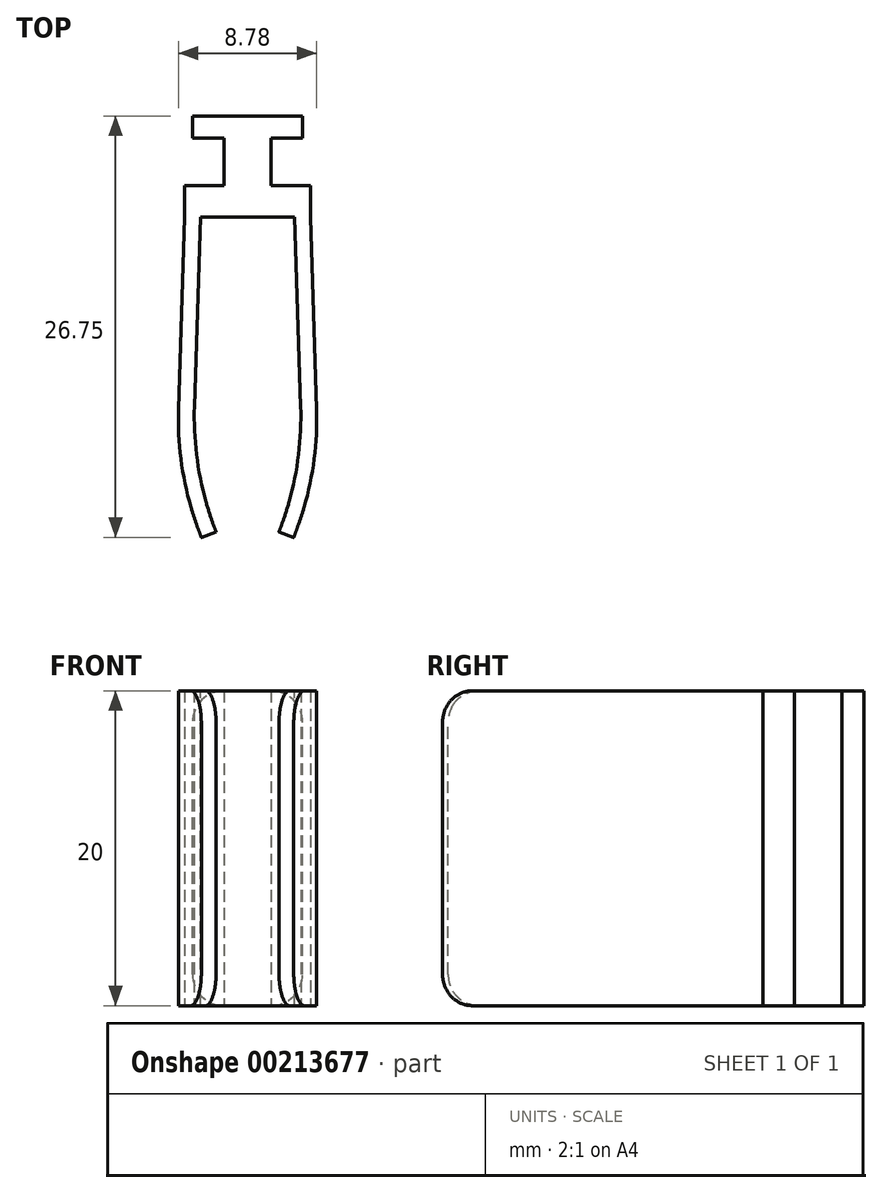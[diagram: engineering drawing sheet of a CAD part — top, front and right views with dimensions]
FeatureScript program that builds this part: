
annotation { "Feature Type Name" : "Feature", "Feature Type Description" : "" }
export const myFeature = defineFeature(function(context is Context, id is Id, definition is map)
    precondition{}
    {
        {
            var Q0;
            Q0=qCreatedBy(makeId("Front.planeOp"),FACE);
            var sketch = newSketch(context, id + "F0", { "sketchPlane" : qUnion([Q0])});
            skLineSegment(sketch, "E0.bottom", {"start": v(3.5, -10) * mm, "end": v(-3.5, -10) * mm});
            skLineSegment(sketch, "E0.top", {"start": v(3.5, 10) * mm, "end": v(-3.5, 10) * mm});
            skLineSegment(sketch, "E0.left", {"start": v(3.5, -10) * mm, "end": v(3.5, 10) * mm});
            skLineSegment(sketch, "E0.right", {"start": v(-3.5, -10) * mm, "end": v(-3.5, 10) * mm});
            skPoint(sketch, "E0.middle", {"position": v(0, 0) * mm});
            skSolve(sketch);
        }
        {
            var Q0;
            Q0=makeQuery(id+"F0.imprint","IMPRINT",FACE,{"disambiguationData":[TD([[makeQuery(id+"F0.imprint","IMPRINT",EDGE,{"derivedFrom":sQuery(id+"F0.wireOp",EDGE,"E0.bottom")}),-1.0]])]});
            extrude(context, id + "F1", {"entities" : qUnion([Q0]), "depth" : 1.4 * mm});
        }
        {
            var Q0;
            Q0=makeQuery(id+"F1.opExtrude","CAP_FACE",FACE,{"disambiguationData":[OSD([sQuery(id+"F0.wireOp",EDGE,"E0.bottom"),sQuery(id+"F0.wireOp",EDGE,"E0.top"),sQuery(id+"F0.wireOp",EDGE,"E0.left"),sQuery(id+"F0.wireOp",EDGE,"E0.right")])],"isStart":false});
            var sketch = newSketch(context, id + "F2", { "sketchPlane" : qUnion([Q0])});
            skLineSegment(sketch, "E1.bottom", {"start": v(1.5, 10) * mm, "end": v(-1.5, 10) * mm});
            skLineSegment(sketch, "E1.top", {"start": v(1.5, -10) * mm, "end": v(-1.5, -10) * mm});
            skLineSegment(sketch, "E1.left", {"start": v(1.5, 10) * mm, "end": v(1.5, -10) * mm});
            skLineSegment(sketch, "E1.right", {"start": v(-1.5, 10) * mm, "end": v(-1.5, -10) * mm});
            skPoint(sketch, "E1.middle", {"position": v(0, 0) * mm});
            skSolve(sketch);
        }
        {
            var Q0;
            Q0=makeQuery(id+"F2.imprint","IMPRINT",FACE,{"disambiguationData":[TD([[makeQuery(id+"F2.imprint","IMPRINT",EDGE,{"derivedFrom":sQuery(id+"F2.wireOp",EDGE,"E1.bottom")}),1.0]])]});
            extrude(context, id + "F3", {"entities" : qUnion([Q0]), "operationType" : NewBodyOperationType.ADD, "depth" : 3 * mm});
        }
        {
            var Q0;
            Q0=makeQuery(id+"F3.opExtrude","CAP_FACE",FACE,{"disambiguationData":[OSD([sQuery(id+"F2.wireOp",EDGE,"E1.bottom"),sQuery(id+"F2.wireOp",EDGE,"E1.top"),sQuery(id+"F2.wireOp",EDGE,"E1.left"),sQuery(id+"F2.wireOp",EDGE,"E1.right")])],"isStart":false});
            var sketch = newSketch(context, id + "F4", { "sketchPlane" : qUnion([Q0])});
            skLineSegment(sketch, "E2.bottom", {"start": v(4, 10) * mm, "end": v(-4, 10) * mm});
            skLineSegment(sketch, "E2.top", {"start": v(4, -10) * mm, "end": v(-4, -10) * mm});
            skLineSegment(sketch, "E2.left", {"start": v(4, 10) * mm, "end": v(4, -10) * mm});
            skLineSegment(sketch, "E2.right", {"start": v(-4, 10) * mm, "end": v(-4, -10) * mm});
            skPoint(sketch, "E2.middle", {"position": v(0, 0) * mm});
            skSolve(sketch);
        }
        {
            var Q0;
            Q0 = qSketchRegion(id + "F4", true);
            extrude(context, id + "F5", {"entities" : qUnion([Q0]), "operationType" : NewBodyOperationType.ADD, "depth" : 2 * mm});
        }
        {
            var Q0;
            Q0=makeQuery(id+"F1.opExtrude","SWEPT_EDGE",EDGE,{"disambiguationData":[OSD([sQuery(id+"F0.wireOp",EDGE,"E0.top"),sQuery(id+"F0.wireOp",EDGE,"E0.left")])]});
            var Q1;
            Q1=makeQuery(id+"F1.opExtrude","SWEPT_EDGE",EDGE,{"disambiguationData":[OSD([sQuery(id+"F0.wireOp",EDGE,"E0.top"),sQuery(id+"F0.wireOp",EDGE,"E0.right")])]});
            var Q2;
            Q2=makeQuery(id+"F1.opExtrude","SWEPT_EDGE",EDGE,{"disambiguationData":[OSD([sQuery(id+"F0.wireOp",EDGE,"E0.bottom"),sQuery(id+"F0.wireOp",EDGE,"E0.left")])]});
            var Q3;
            Q3=makeQuery(id+"F1.opExtrude","SWEPT_EDGE",EDGE,{"disambiguationData":[OSD([sQuery(id+"F0.wireOp",EDGE,"E0.bottom"),sQuery(id+"F0.wireOp",EDGE,"E0.right")])]});
            fillet(context, id + "F6", {"entities" : qUnion([Q0, Q1, Q2, Q3]), "radius" : 2 * mm, "tangentPropagation" : true, "allowEdgeOverflow" : false});
        }
        {
            var Q0;
            Q0=makeQuery(id+"F5.boolean.opBoolean","MERGE",FACE,{"derivedFrom":[makeQuery(id+"F3.boolean.opBoolean","MERGE",FACE,{"derivedFrom":[makeQuery(id+"F1.opExtrude","SWEPT_FACE",FACE,{"disambiguationData":[OSD([sQuery(id+"F0.wireOp",EDGE,"E0.top")])]}),makeQuery(id+"F3.opExtrude","SWEPT_FACE",FACE,{"disambiguationData":[OSD([sQuery(id+"F2.wireOp",EDGE,"E1.bottom")])]})]}),makeQuery(id+"F5.opExtrude","SWEPT_FACE",FACE,{"disambiguationData":[OSD([sQuery(id+"F4.wireOp",EDGE,"E2.bottom")])]})]});
            var sketch = newSketch(context, id + "F7", { "sketchPlane" : qUnion([Q0])});
            skLineSegment(sketch, "E3", {"start": v(-4, -6.4) * mm, "end": v(-4.5, -22.57) * mm});
            skLineSegment(sketch, "E4", {"start": v(0, -6.4) * mm, "end": v(0, -33.51) * mm, "construction": true});
            skPoint(sketch, "E4.endSnap0", {"position": v(0, -6.4) * mm});
            skLineSegment(sketch, "E5.MirrorCS", {"start": v(4, -6.4) * mm, "end": v(4.5, -22.57) * mm});
            skLineSegment(sketch, "E6", {"start": v(-4.5, -22.57) * mm, "end": v(-2.94, -26.75) * mm});
            skLineSegment(sketch, "E7", {"start": v(-2.94, -26.75) * mm, "end": v(-2, -26.4) * mm});
            skLineSegment(sketch, "E8", {"start": v(-2, -26.4) * mm, "end": v(-3.5, -22.4) * mm});
            skLineSegment(sketch, "E9", {"start": v(-3.5, -22.4) * mm, "end": v(-3, -6.4) * mm});
            skLineSegment(sketch, "E10.MirrorCS", {"start": v(3.5, -22.4) * mm, "end": v(3, -6.4) * mm});
            skLineSegment(sketch, "E11.MirrorCS", {"start": v(2, -26.4) * mm, "end": v(3.5, -22.4) * mm});
            skLineSegment(sketch, "E12.MirrorCS", {"start": v(2.94, -26.75) * mm, "end": v(2, -26.4) * mm});
            skLineSegment(sketch, "E13.MirrorCS", {"start": v(4.5, -22.57) * mm, "end": v(2.94, -26.75) * mm});
            skLineSegment(sketch, "E14", {"start": v(-3, -6.4) * mm, "end": v(-4, -6.4) * mm});
            skSolve(sketch);
        }
        {
            var Q0;
            Q0=makeQuery(id+"F7.imprint","IMPRINT",FACE,{"disambiguationData":[TD([[makeQuery(id+"F7.imprint","IMPRINT",EDGE,{"derivedFrom":sQuery(id+"F7.wireOp",EDGE,"E3")}),1.0]])]});
            var Q1;
            {var subQ1=sQuery(id+"F7.wireOp",EDGE,"E5.MirrorCS");Q1=makeQuery(id+"F7.imprint","IMPRINT",FACE,{"disambiguationData":[TD([[makeQuery(id+"F7.imprint","IMPRINT",EDGE,{"derivedFrom":subQ1}),-1.0]])]});}
            var Q2;
            Q2=makeQuery(id+"F5.opExtrude","CAP_VERTEX",VERTEX,{"disambiguationData":[OSD([sQuery(id+"F4.wireOp",EDGE,"E2.top"),sQuery(id+"F4.wireOp",EDGE,"E2.right")])],"isStart":false});
            extrude(context, id + "F8", {"entities" : qUnion([Q0, Q1]), "operationType" : NewBodyOperationType.ADD, "endBound" : BoundingType.UP_TO_VERTEX, "oppositeDirection" : true, "endBoundEntityVertex" : qUnion([Q2]), "depth" : 25 * mm});
        }
        {
            var Q0;
            Q0=makeQuery(id+"F8.opExtrude","SWEPT_EDGE",EDGE,{"disambiguationData":[OSD([sQuery(id+"F7.wireOp",EDGE,"E8"),sQuery(id+"F7.wireOp",EDGE,"E9")])]});
            var Q1;
            Q1=makeQuery(id+"F8.opExtrude","SWEPT_EDGE",EDGE,{"disambiguationData":[OSD([sQuery(id+"F7.wireOp",EDGE,"E10.MirrorCS"),sQuery(id+"F7.wireOp",EDGE,"E11.MirrorCS")])]});
            var Q2;
            Q2=makeQuery(id+"F8.opExtrude","SWEPT_EDGE",EDGE,{"disambiguationData":[OSD([sQuery(id+"F7.wireOp",EDGE,"E5.MirrorCS"),sQuery(id+"F7.wireOp",EDGE,"E13.MirrorCS")])]});
            var Q3;
            Q3=makeQuery(id+"F8.opExtrude","SWEPT_EDGE",EDGE,{"disambiguationData":[OSD([sQuery(id+"F7.wireOp",EDGE,"E3"),sQuery(id+"F7.wireOp",EDGE,"E6")])]});
            fillet(context, id + "F9", {"entities" : qUnion([Q0, Q1, Q2, Q3]), "radius" : 20 * mm, "tangentPropagation" : true, "allowEdgeOverflow" : false});
        }
        {
            var Q0;
            Q0=makeQuery(id+"F8.opExtrude","CAP_EDGE",EDGE,{"disambiguationData":[OSD([sQuery(id+"F7.wireOp",EDGE,"E7")])],"isStart":true});
            var Q1;
            Q1=makeQuery(id+"F8.opExtrude","CAP_EDGE",EDGE,{"disambiguationData":[OSD([sQuery(id+"F7.wireOp",EDGE,"E12.MirrorCS")])],"isStart":true});
            var Q2;
            Q2=makeQuery(id+"F8.opExtrude","CAP_EDGE",EDGE,{"disambiguationData":[OSD([sQuery(id+"F7.wireOp",EDGE,"E7")])],"isStart":false});
            var Q3;
            Q3=makeQuery(id+"F8.opExtrude","CAP_EDGE",EDGE,{"disambiguationData":[OSD([sQuery(id+"F7.wireOp",EDGE,"E12.MirrorCS")])],"isStart":false});
            fillet(context, id + "F10", {"entities" : qUnion([Q0, Q1, Q2, Q3]), "radius" : 2 * mm, "tangentPropagation" : true, "allowEdgeOverflow" : false});
        }
    });
